# Revit family: Countertop-120cm-WithoutFaucetHole-Left-Vitra-OriginSeries-65722+65723+65724
name_source: partatom
category: Furniture Systems
revit_build: Autodesk Revit 2017 (Build: 20160225_1515(x64)
units: mm (PartAtom-declared; Revit-internal decimal feet)

## family parameters
Cut with Voids When Loaded = No
Host = Face
OmniClass Number = 23.40.00.00
OmniClass Title = Equipment and Furnishings
Part Type = Normal
Room Calculation Point = No
Round Connector Dimension = Use Diameter
Shared = Yes

## types (3) — shared parameters
BIMobject category = Countertops
Brand = VitrA
Default Elevation = 850 mm  [stored 2.78871 ft]
Design country = Turkey
IFC Classification = Furnishing Element
Installation instructions = https://www.vitraglobal.com
Main Material = Glass
Manufacturer = VitrA
Manufacturer name = VitrA
Masterformat 2014 Code = 12 36 00
Masterformat 2014 Description = Countertops
Mounting type = Top Counter
NBS Referans Code = 35-12-18
NBS Referans Description = Counter Tops
Nominal Depth (mm) = 480 mm
Nominal Height (mm) = 12 mm  [stored 0.0393701 ft]
Nominal Width (mm) = 1205 mm  [stored 3.95341 ft]
OmniClass Code = 23-21 19 17
OmniClass Description = Casework Component Work Surfaces
Product Guid = https://www.vitraglobal.com
Product certification = https://www.vitraglobal.com
Product family = Origin
Product group = Counters - Standard Workbenches - Top Counter
>
Product url = https://www.vitraglobal.com
Technical description = https://www.vitraglobal.com
URL = https://vitraglobal.com
Uniclass 1.4 Code = L8571
Uniclass 1.4 Description = Counters
Uniclass 2.0 Code = PR-35-12-18
Uniclass 2.0 Description = Counter Tops
Uniclass 2015 Code = Pr_40_30_30_18
Uniclass 2015 Name = Counter tops
Uniformat II Code = C30
Uniformat II Description = INTERIOR FINISHES
Warranty Period (Year) = 2
Youtube = https://www.youtube.com

## per-type parameters (varying)
| type | Article No. (default) | Color | Description | Model | Primary Material | Product SKU |
| Countertop-120cm-WithLeftSyphonHole-Vitra-OriginSeries-65722 | 65722 | White | Origin Top counter - with left syphon hole - without faucet hole - 120cm - White | 65722 | White Glass | 65722 |
| Countertop-120cm-WithLeftSyphonHole-Vitra-OriginSeries-65723 | 65723 | Black | Origin Top counter - with left syphon hole - without faucet hole 120cm - Black | 65723 | Black Glass | 65723 |
| Countertop-120cm-WithLeftSyphonHole-Vitra-OriginSeries-65724 | 65724 | Neolith | Origin Top counter - with left syphon hole - without faucet hole - 120cm - Neolith | 65724 | Neolith | 65724 |

note: [stored X ft] marks values corroborated as IEEE doubles in the binary element streams (Revit-internal decimal feet)

## geometry (parser evidence)
native form markers: Sweep x3
no freeform markers — native parametric forms only
